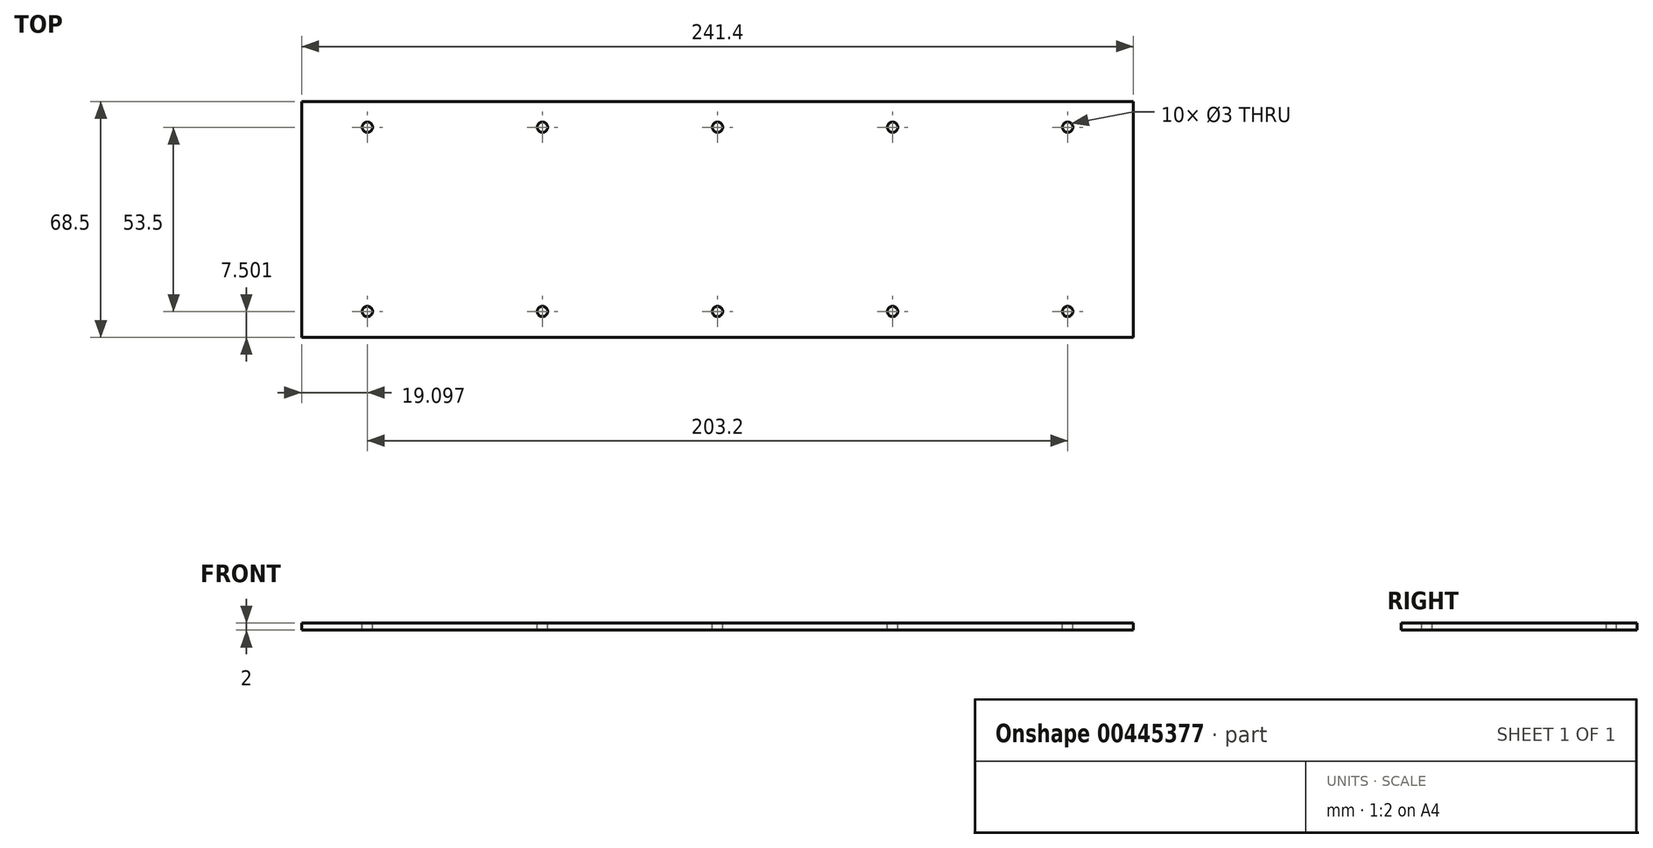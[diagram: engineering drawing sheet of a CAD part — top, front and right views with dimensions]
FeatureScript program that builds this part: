
annotation { "Feature Type Name" : "Feature", "Feature Type Description" : "" }
export const myFeature = defineFeature(function(context is Context, id is Id, definition is map)
    precondition{}
    {
        {
            var Q0;
            Q0=qCreatedBy(makeId("Top.planeOp"),FACE);
            var sketch = newSketch(context, id + "F0", { "sketchPlane" : qUnion([Q0])});
            skLineSegment(sketch, "E0.bottom", {"start": v(-102.06, 9.02) * mm, "end": v(139.34, 9.02) * mm});
            skLineSegment(sketch, "E0.top", {"start": v(-102.06, -59.48) * mm, "end": v(139.34, -59.48) * mm});
            skLineSegment(sketch, "E0.left", {"start": v(-102.06, 9.02) * mm, "end": v(-102.06, -59.48) * mm});
            skLineSegment(sketch, "E0.right", {"start": v(139.34, 9.02) * mm, "end": v(139.34, -59.48) * mm});
            skSolve(sketch);
        }
        {
            var Q0;
            Q0=qSketchRegion(id+"F0",true);
            extrude(context, id + "F1", {"entities" : qUnion([Q0]), "depth" : 2 * mm});
        }
        {
            var Q0;
            Q0=makeQuery(id+"F1.opExtrude","CAP_FACE",FACE,{"disambiguationData":[OSD([sQuery(id+"F0.wireOp",EDGE,"E0.bottom"),sQuery(id+"F0.wireOp",EDGE,"E0.top"),sQuery(id+"F0.wireOp",EDGE,"E0.left"),sQuery(id+"F0.wireOp",EDGE,"E0.right")])],"isStart":false});
            var sketch = newSketch(context, id + "F2", { "sketchPlane" : qUnion([Q0])});
            skLineSegment(sketch, "E1", {"start": v(-103.4, 1.52) * mm, "end": v(112.3, 1.52) * mm});
            skLineSegment(sketch, "E2", {"start": v(-82.18, 1.52) * mm, "end": v(-82.18, 9.02) * mm});
            skCircle(sketch, "E3", {"center": v(-82.96, 1.52) * mm, "radius": 1.5 * mm});
            skCircle(sketch, "E4.1.0.0", {"center": v(-32.16, 1.52) * mm, "radius": 1.5 * mm});
            skCircle(sketch, "E4.2.0.0", {"center": v(18.64, 1.52) * mm, "radius": 1.5 * mm});
            skCircle(sketch, "E4.3.0.0", {"center": v(69.44, 1.52) * mm, "radius": 1.5 * mm});
            skCircle(sketch, "E4.4.0.0", {"center": v(120.24, 1.52) * mm, "radius": 1.5 * mm});
            skLineSegment(sketch, "E4.direction1", {"start": v(-82.96, 1.52) * mm, "end": v(-32.16, 1.52) * mm, "construction": true});
            skLineSegment(sketch, "E5", {"start": v(18.64, 9.02) * mm, "end": v(18.64, -59.48) * mm, "construction": true});
            skLineSegment(sketch, "E6", {"start": v(0, 0) * mm, "end": v(2.92, 0) * mm});
            skLineSegment(sketch, "E7", {"start": v(-102.06, -25.23) * mm, "end": v(139.34, -25.23) * mm});
            skCircle(sketch, "E8.MirrorC", {"center": v(120.24, -51.98) * mm, "radius": 1.5 * mm});
            skCircle(sketch, "E9.MirrorC", {"center": v(69.44, -51.98) * mm, "radius": 1.5 * mm});
            skCircle(sketch, "E10.MirrorC", {"center": v(18.64, -51.98) * mm, "radius": 1.5 * mm});
            skCircle(sketch, "E11.MirrorC", {"center": v(-32.16, -51.98) * mm, "radius": 1.5 * mm});
            skCircle(sketch, "E12.MirrorC", {"center": v(-82.96, -51.98) * mm, "radius": 1.5 * mm});
            skSolve(sketch);
        }
        {
            var Q0;
            Q0=qSketchRegion(id+"F2",true);
            extrude(context, id + "F3", {"entities" : qUnion([Q0]), "operationType" : NewBodyOperationType.REMOVE, "endBound" : BoundingType.THROUGH_ALL, "oppositeDirection" : true, "depth" : 25.4 * mm});
        }
    });
